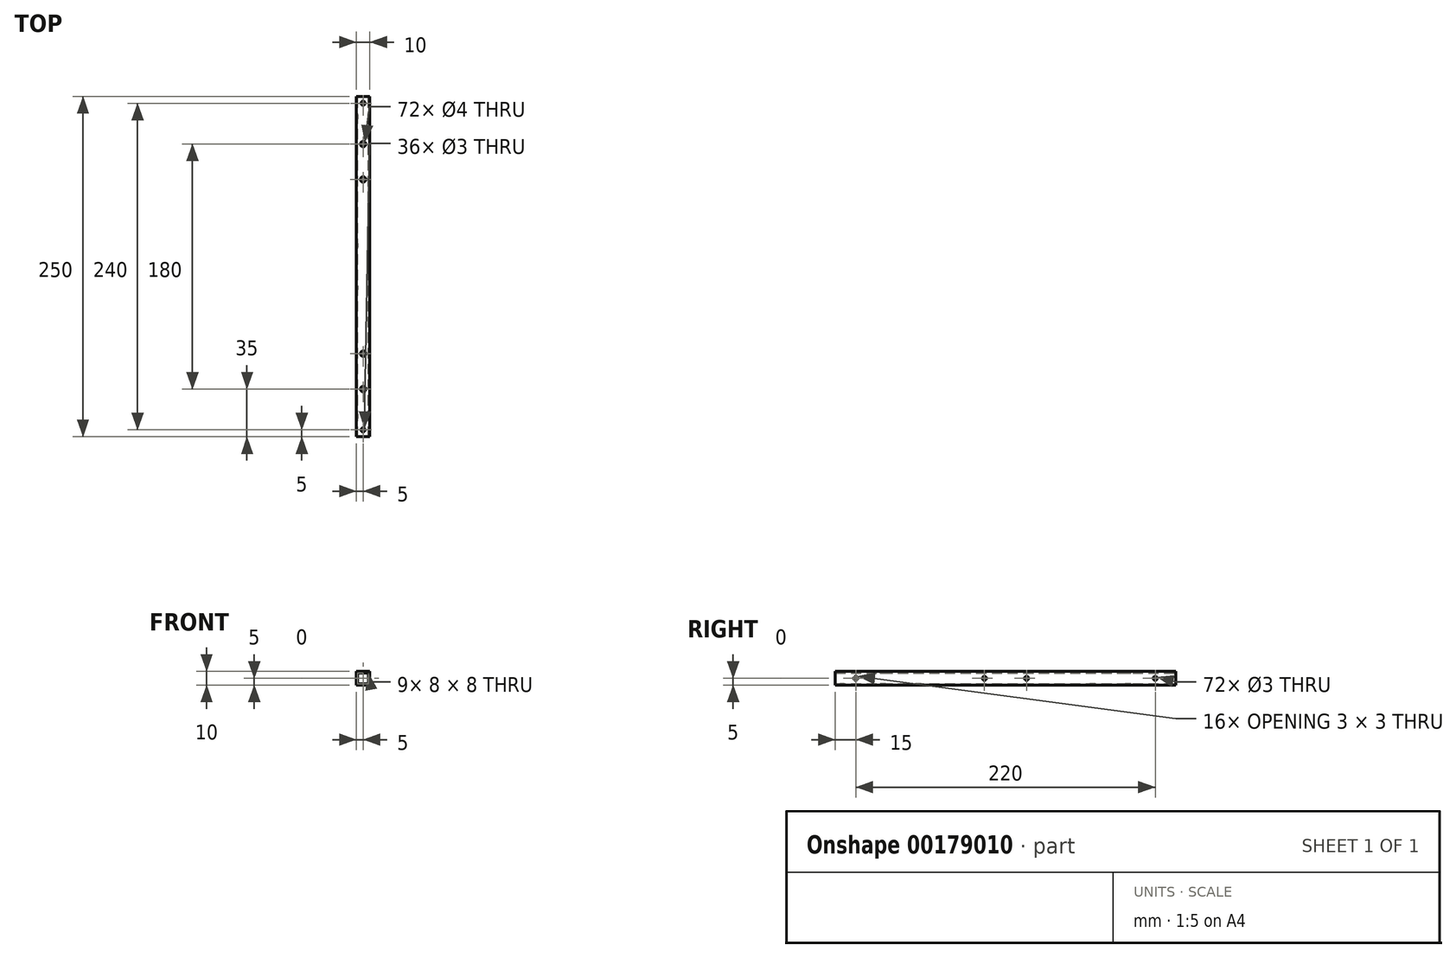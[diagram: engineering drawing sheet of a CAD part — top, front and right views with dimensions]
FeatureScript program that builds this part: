
annotation { "Feature Type Name" : "Feature", "Feature Type Description" : "" }
export const myFeature = defineFeature(function(context is Context, id is Id, definition is map)
    precondition{}
    {
        {
            var Q0;
            Q0=qCreatedBy(makeId("Front.planeOp"),FACE);
            var sketch = newSketch(context, id + "F0", { "sketchPlane" : qUnion([Q0])});
            skLineSegment(sketch, "E0.bottom", {"start": v(-5, -5) * mm, "end": v(5, -5) * mm});
            skLineSegment(sketch, "E0.top", {"start": v(-5, 5) * mm, "end": v(5, 5) * mm});
            skLineSegment(sketch, "E0.left", {"start": v(-5, -5) * mm, "end": v(-5, 5) * mm});
            skLineSegment(sketch, "E0.right", {"start": v(5, -5) * mm, "end": v(5, 5) * mm});
            skPoint(sketch, "E0.middle", {"position": v(0, 0) * mm});
            skLineSegment(sketch, "E1.bottom", {"start": v(-4, -4) * mm, "end": v(4, -4) * mm});
            skLineSegment(sketch, "E1.top", {"start": v(-4, 4) * mm, "end": v(4, 4) * mm});
            skLineSegment(sketch, "E1.left", {"start": v(-4, -4) * mm, "end": v(-4, 4) * mm});
            skLineSegment(sketch, "E1.right", {"start": v(4, -4) * mm, "end": v(4, 4) * mm});
            skSolve(sketch);
        }
        {
            var Q0;
            Q0 = qSketchRegion(id + "F0", true);
            extrude(context, id + "F1", {"entities" : qUnion([Q0]), "depth" : 250 * mm});
        }
        {
            var Q0;
            Q0=makeQuery(id+"F1.opExtrude","SWEPT_FACE",FACE,{"disambiguationData":[OSD([sQuery(id+"F0.wireOp",EDGE,"E0.right")])]});
            var sketch = newSketch(context, id + "F2", { "sketchPlane" : qUnion([Q0])});
            skLineSegment(sketch, "E2", {"start": v(-250, 0) * mm, "end": v(0, 0) * mm, "construction": true});
            skLineSegment(sketch, "E3", {"start": v(-125, 5) * mm, "end": v(-125, -5) * mm, "construction": true});
            skCircle(sketch, "E4", {"center": v(-140.5, 0) * mm, "radius": 1.5 * mm});
            skCircle(sketch, "E5", {"center": v(-235, 0) * mm, "radius": 1.5 * mm});
            skLineSegment(sketch, "E6.MirrorCS", {"start": v(0, 0) * mm, "end": v(-250, 0) * mm, "construction": true});
            skCircle(sketch, "E7.MirrorC", {"center": v(-15, 0) * mm, "radius": 1.5 * mm});
            skCircle(sketch, "E8.MirrorC", {"center": v(-109.5, 0) * mm, "radius": 1.5 * mm});
            skSolve(sketch);
        }
        {
            var Q0;
            Q0=makeQuery(id+"F1.opExtrude","SWEPT_FACE",FACE,{"disambiguationData":[OSD([sQuery(id+"F0.wireOp",EDGE,"E0.top")])]});
            var sketch = newSketch(context, id + "F3", { "sketchPlane" : qUnion([Q0])});
            skLineSegment(sketch, "E9", {"start": v(0, 0) * mm, "end": v(0, -250) * mm, "construction": true});
            skLineSegment(sketch, "E10", {"start": v(5, -125) * mm, "end": v(-5, -125) * mm, "construction": true});
            skCircle(sketch, "E11", {"center": v(0, -245) * mm, "radius": 1.5 * mm});
            skCircle(sketch, "E12", {"center": v(0, -215) * mm, "radius": 2 * mm});
            skCircle(sketch, "E13", {"center": v(0, -189) * mm, "radius": 2 * mm});
            skCircle(sketch, "E14.MirrorC", {"center": v(0, -61) * mm, "radius": 2 * mm});
            skCircle(sketch, "E15.MirrorC", {"center": v(0, -35) * mm, "radius": 2 * mm});
            skCircle(sketch, "E16.MirrorC", {"center": v(0, -5) * mm, "radius": 1.5 * mm});
            skSolve(sketch);
        }
        {
            var Q0;
            Q0 = qSketchRegion(id + "F2", true);
            extrude(context, id + "F4", {"entities" : qUnion([Q0]), "operationType" : NewBodyOperationType.REMOVE, "oppositeDirection" : true, "depth" : 25 * mm});
        }
        {
            var Q0;
            Q0 = qSketchRegion(id + "F3", true);
            extrude(context, id + "F5", {"entities" : qUnion([Q0]), "operationType" : NewBodyOperationType.REMOVE, "oppositeDirection" : true, "depth" : 25 * mm});
        }
    });
